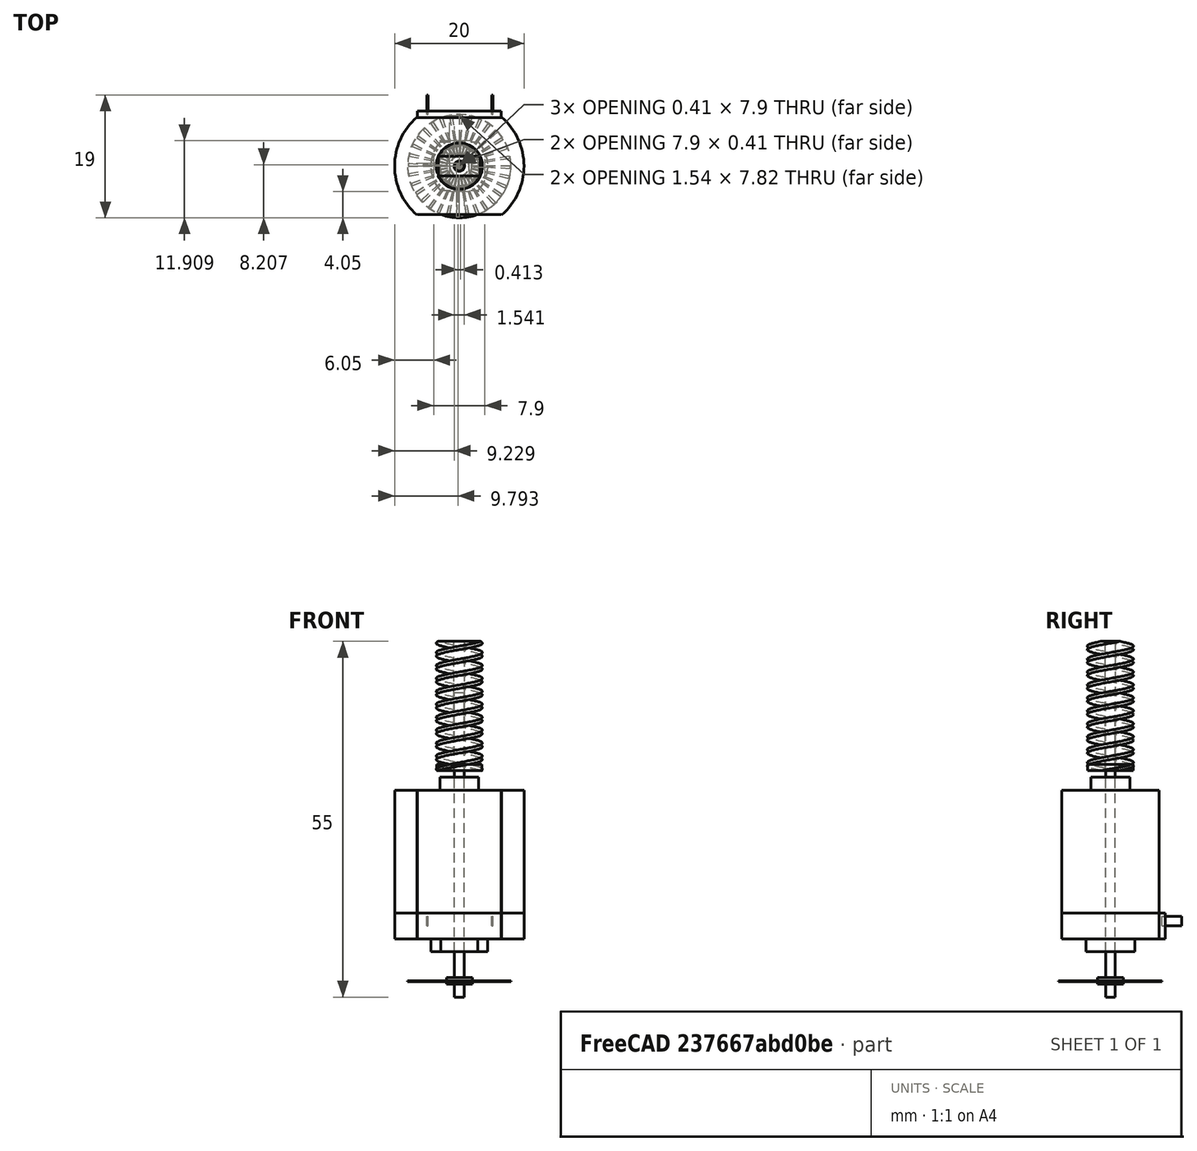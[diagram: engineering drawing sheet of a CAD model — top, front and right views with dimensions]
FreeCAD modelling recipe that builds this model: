
FCSTD DOCUMENT  (FreeCAD 0.15R4671 (Git))
Label: DCMotorMabuchi14WormEncoder
License: CreativeCommons Attribution-NonCommercial
LicenseURL: http://creativecommons.org/licenses/by-nc/4.0/
objects: Part::Cylinder×4, Part::Feature×3, Part::Box×2, Part::Compound×2, Part::Cut×1, Sketcher::SketchObject×1, PartDesign::Pocket×1, PartDesign::PolarPattern×1
note: 16 computed .brp shape members not serialized (recipe doc carries the construction recipe); baked Part::Feature solids carry a one-line shape summary decoded from their .brp

FEATURE [Part::Feature] Fusion_solid002  label="MotorBodyMetal"
  shape: bbox 20 x 15.09 x 21 mm, 16 faces (baked)
FEATURE [Part::Cylinder] Cylinder  label="MotorAxisShaft"
  Angle = 360
  Height = 47
  Placement = pos=(0,0,-5) rot=(0,0,1;0rad)
  Radius = 0.75
FEATURE [Part::Feature] Fusion001  label="MotorBodyPlastic"
  shape: bbox 20 x 16.05 x 6 mm, 27 faces (baked)
FEATURE [Part::Box] Box  label="MotorPinA"
  Height = 1.5
  Length = 0.2
  Placement = pos=(5,8,6) rot=(0,0,1;0rad)
  Width = 3
FEATURE [Part::Box] Box001  label="MotorPinB"
  Height = 1.5
  Length = 0.2
  Placement = pos=(-5,8,6) rot=(0,0,1;0rad)
  Width = 3
FEATURE [Part::Feature] Fusion_solid  label="Fusion (Solid)001"
  shape: bbox 10.12 x 11.2 x 20 mm, 30 faces (baked)
FEATURE [Part::Cylinder] Cylinder001  label="AxisHole"
  Angle = 360
  Height = 23
  Placement = pos=(0,0,-1) rot=(0,0,1;0rad)
  Radius = 0.8
FEATURE [Part::Cut] Cut  label="WormPlastic"
  Base = -> Fusion_solid
  Placement = pos=(0,0,30) rot=(0,0,1;0rad)
  Tool = -> Cylinder001
FEATURE [Part::Cylinder] Cylinder002  label="EncoderBrass"
  Angle = 360
  Height = 1
  Placement = pos=(0,0,-3) rot=(0,0,1;0rad)
  Radius = 2
FEATURE [Part::Cylinder] Cylinder003  label="EncoderDisk"
  Angle = 360
  Height = 0.1
  Placement = pos=(0,0,-2.6) rot=(0,0,1;0rad)
  Radius = 8
FEATURE [Sketcher::SketchObject] Sketch001
  Placement = pos=(0,0,-2.5) rot=(0,0,1;0rad)
  Support = -> Cylinder003 [Face2]
  sketch-geometry (3):
    g0: ArcOfCircle CenterX=0 CenterY=0 CenterZ=0 NormalX=0 NormalY=0 NormalZ=1 Radius=7.9 StartAngle=1.51844 EndAngle=1.5708
    g1: LineSegment StartX=0 StartY=7.9 StartZ=0 EndX=0 EndY=0 EndZ=0
    g2: LineSegment StartX=0.413454 StartY=7.88917 StartZ=0 EndX=0 EndY=0 EndZ=0
  constraints (8):
    c: Coincident(g0,g-1)
    c: Coincident(g1,g0)
    c: Coincident(g1,g-1)
    c: Coincident(g2,g0)
    c: Coincident(g2,g-1)
    c: Angle(g1) = -1.5708
    c: Angle(g2) = -1.62316
    c: Radius(g0) = 7.9
FEATURE [PartDesign::Pocket] Pocket
  Length = 5
  Placement = pos=(0,0,-2.6) rot=(0,0,1;0rad)
  Sketch = -> Sketch001
  Type = 1
FEATURE [PartDesign::PolarPattern] PolarPattern
  Angle = 360
  Axis = -> Sketch001 [N_Axis]
  Occurrences = 32
  Originals = -> [Pocket]
  Placement = pos=(0,0,-2.6) rot=(0,0,1;0rad)
FEATURE [Part::Compound] Compound  label="CodeWheel"
  Links = -> [Cylinder002,Cylinder003,Pocket,PolarPattern]
FEATURE [Part::Compound] Compound001  label="Connector"
  Links = -> [Box,Box001]
